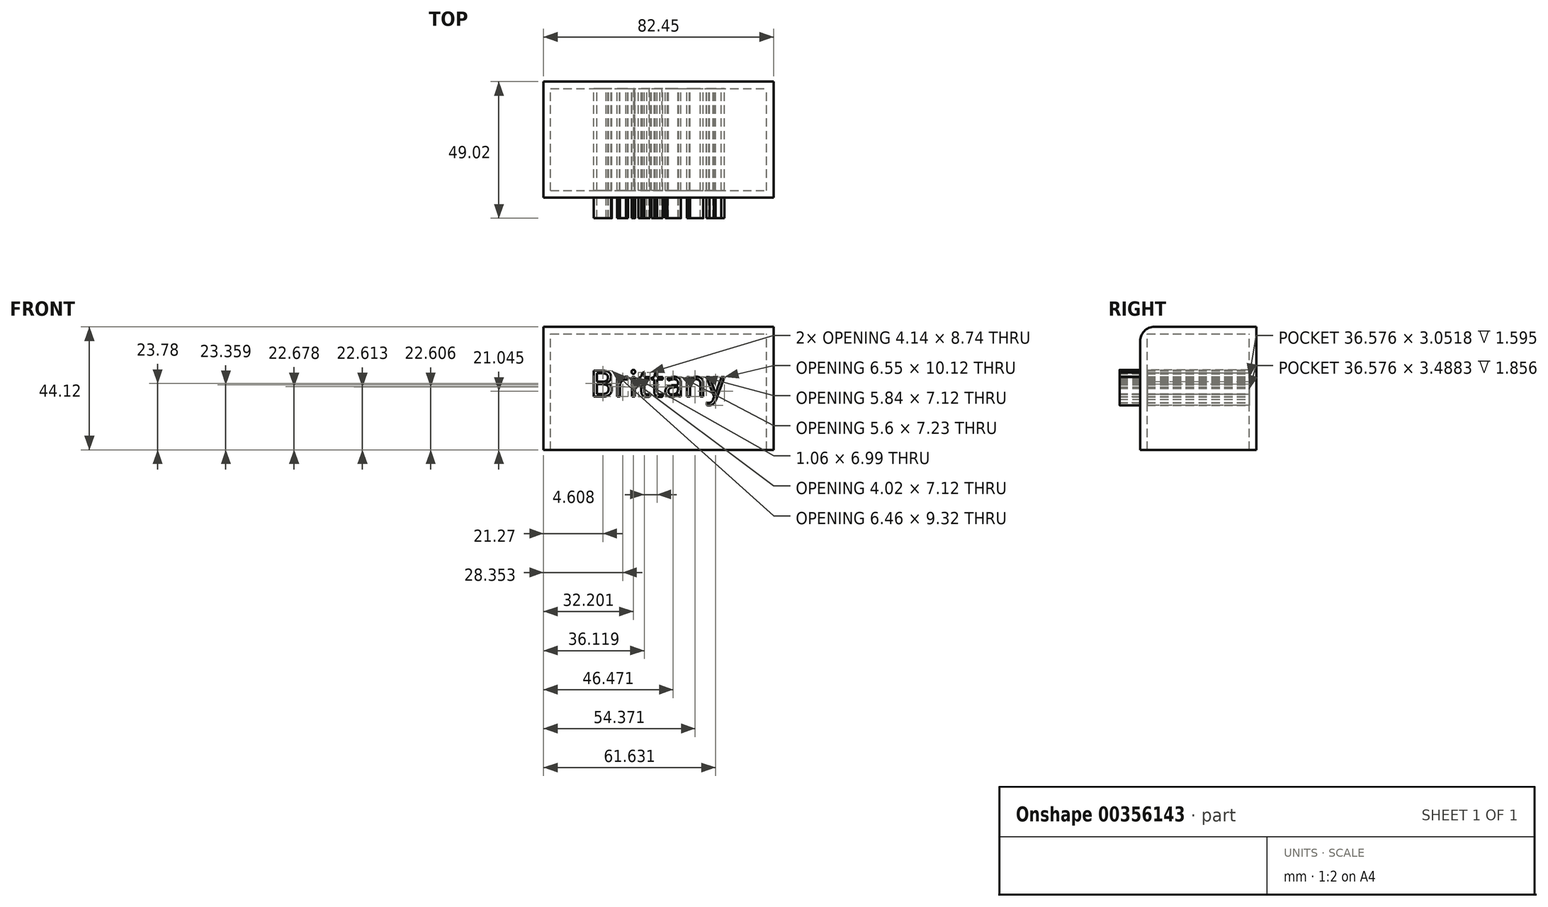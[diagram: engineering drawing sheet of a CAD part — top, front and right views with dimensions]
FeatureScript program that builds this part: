
annotation { "Feature Type Name" : "Feature", "Feature Type Description" : "" }
export const myFeature = defineFeature(function(context is Context, id is Id, definition is map)
    precondition{}
    {
        {
            var Q0;
            Q0=qCreatedBy(makeId("Front.planeOp"),FACE);
            var sketch = newSketch(context, id + "F0", { "sketchPlane" : qUnion([Q0])});
            skLineSegment(sketch, "E0.bottom", {"start": v(0, 0) * mm, "end": v(82.45, 0) * mm});
            skLineSegment(sketch, "E0.top", {"start": v(0, 44.12) * mm, "end": v(82.45, 44.12) * mm});
            skLineSegment(sketch, "E0.left", {"start": v(0, 0) * mm, "end": v(0, 44.12) * mm});
            skLineSegment(sketch, "E0.right", {"start": v(82.45, 0) * mm, "end": v(82.45, 44.12) * mm});
            skSolve(sketch);
        }
        {
            var Q0;
            Q0=makeQuery(id+"F0.imprint","IMPRINT",FACE,{"disambiguationData":[TD([[makeQuery(id+"F0.imprint","IMPRINT",EDGE,{"derivedFrom":sQuery(id+"F0.wireOp",EDGE,"E0.bottom")}),1.0]])]});
            extrude(context, id + "F1", {"entities" : qUnion([Q0]), "depth" : 41.66 * mm});
        }
        {
            var Q0;
            Q0=makeQuery(id+"F1.opExtrude","SWEPT_FACE",FACE,{"disambiguationData":[OSD([sQuery(id+"F0.wireOp",EDGE,"E0.bottom")])]});
            shell(context, id + "F2", {"entities" : qUnion([Q0]), "thickness" : 2.54 * mm});
        }
        {
            var Q0;
            Q0=makeQuery(id+"F1.opExtrude","CAP_EDGE",EDGE,{"disambiguationData":[OSD([sQuery(id+"F0.wireOp",EDGE,"E0.top")])],"isStart":false});
            fillet(context, id + "F3", {"entities" : qUnion([Q0]), "radius" : 5.08 * mm, "tangentPropagation" : true, "allowEdgeOverflow" : false});
        }
        {
            var Q0;
            Q0=qCreatedBy(makeId("Front.planeOp"),FACE);
            var sketch = newSketch(context, id + "F4", { "sketchPlane" : qUnion([Q0])});
            skText(sketch, "E1", { "text": "Brittany", "fontName": "OpenSans-Regular.ttf"});
            const initialGuessF4  = {"E1": [0.01676, 0.01912, 1, 0, 0.0094]};
            skSetInitialGuess(sketch, initialGuessF4);
            skSolve(sketch);
        }
        {
            var Q0;
            Q0 = qSketchRegion(id + "F4", true);
            extrude(context, id + "F5", {"entities" : qUnion([Q0]), "operationType" : NewBodyOperationType.ADD, "depth" : 49.02 * mm});
        }
    });
